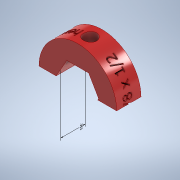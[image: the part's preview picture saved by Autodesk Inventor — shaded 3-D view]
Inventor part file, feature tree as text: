
AUTODESK INVENTOR PART (.ipt)
format: ipt  version: 2022.1 (Build 261234000, 234)  size: 932,864 bytes
history: native  units: in
note: dims shown in document units (in); Inventor stores cm internally (conversion verified against a paired STEP export)
features: sketch x4, other x2, extrude x2, thicken_offset x1, plane x1, emboss x1, hole x1, split x1
ambient origin geometry x8: Origin, YZ Plane, XZ Plane, XY Plane, X Axis, Y Axis, Z Axis, Center Point
bodies: Solid1 (feature_tree)
feature tree (13):
  other  "Annotations"
  extrude  "Extrusion1"  Depth=1.125in
  thicken_offset  "Thicken2"
  plane  "Work Plane1"
  emboss  "Emboss1"
  hole  "Hole1"  [1 undecoded]
  extrude  "Extrusion2"  Depth=0.0225in
  split  "Split1"
  sketch  "Sketch1"  dims[d0=0.5in d2=1.125in]
  sketch  "Sketch2"  dims[d3=0.2738in d4=0.375in d5=0.0in]
  sketch  "Sketch3"  dims[d8=0.0225in d9=0.0225in]
  sketch  "Sketch4"  dims[d17=1.0in d18=0.25in d19=0.1in d20=0.0in d21=0.17in d22=0.75in d23=0.5in d24=0.093in d25=0.5635in d26=1.0in d27=0.8108in d28=0.1763in d29=0.1763in d30=0.191in d31=0.2186in d32=0.0in d14=0.1112in d15=0.3058in d16=0.3525in]
  other  "Linear Dimension 2"
note: 1 required parameter value undecoded (feature->parameter linkage not recoverable at this tier; creation-order binding heuristic only, values carry confidence <= 0.55)
